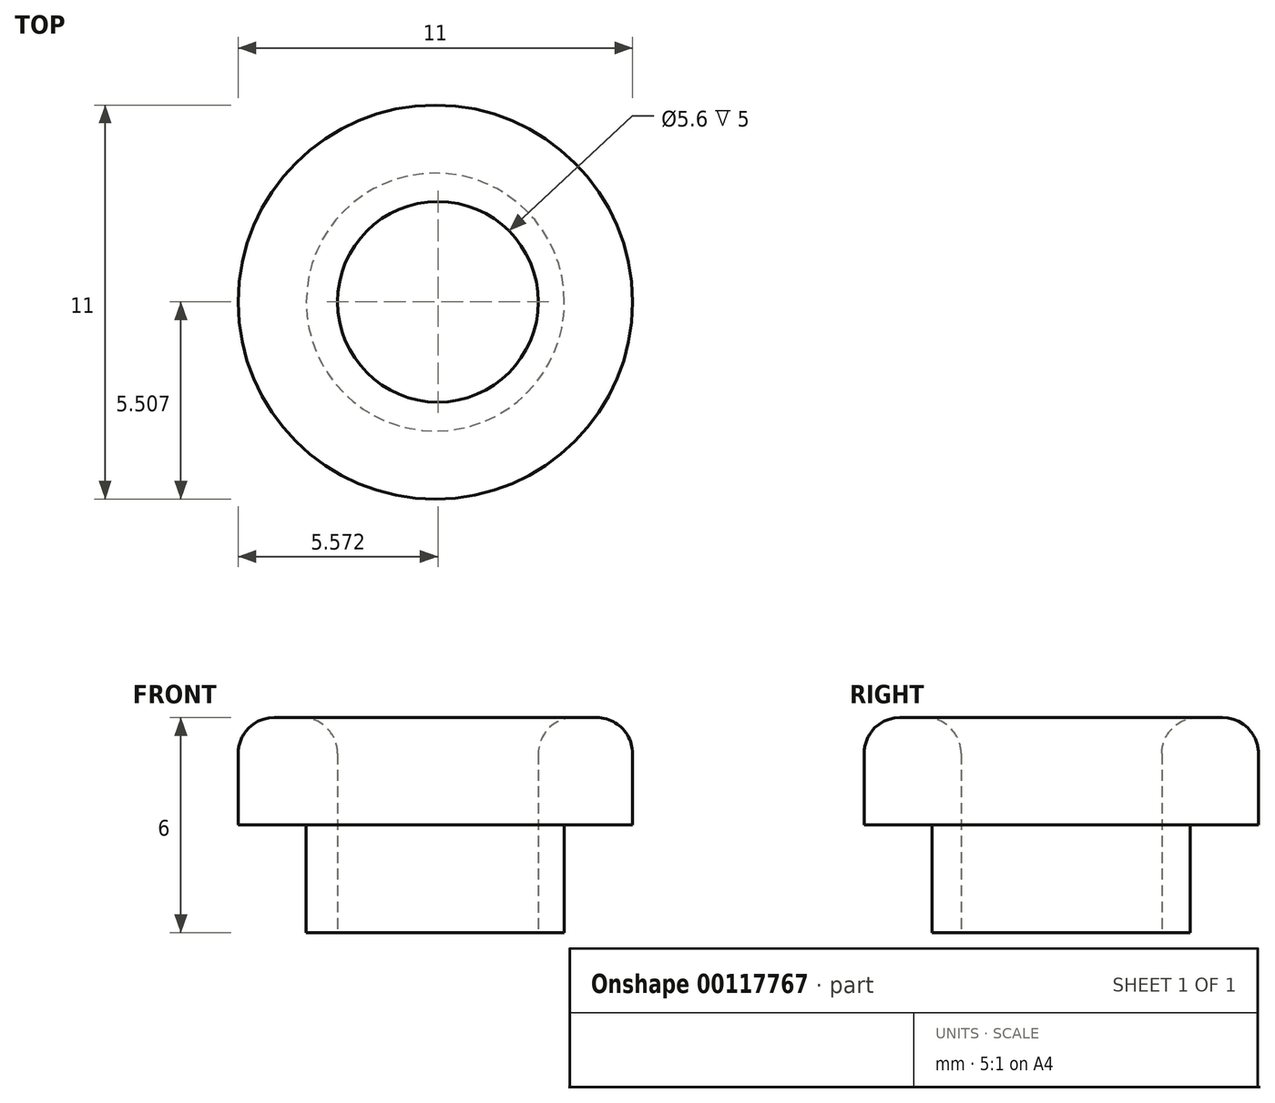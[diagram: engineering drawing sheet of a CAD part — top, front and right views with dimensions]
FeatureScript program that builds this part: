
annotation { "Feature Type Name" : "Feature", "Feature Type Description" : "" }
export const myFeature = defineFeature(function(context is Context, id is Id, definition is map)
    precondition{}
    {
        {
            var Q0;
            Q0=qCreatedBy(makeId("Top.planeOp"),FACE);
            var sketch = newSketch(context, id + "F0", { "sketchPlane" : qUnion([Q0])});
            skCircle(sketch, "E0", {"center": v(0, 0) * mm, "radius": 5.5 * mm});
            skCircle(sketch, "E1", {"center": v(0, 0) * mm, "radius": 3.6 * mm});
            skCircle(sketch, "E2", {"center": v(0.07, 0) * mm, "radius": 2.8 * mm});
            skSolve(sketch);
        }
        {
            var Q0;
            Q0=makeQuery(id+"F0.imprint","IMPRINT",FACE,{"disambiguationData":[TD([[makeQuery(id+"F0.imprint","IMPRINT",EDGE,{"derivedFrom":sQuery(id+"F0.wireOp",EDGE,"E0")}),1.0]])]});
            var Q1;
            Q1=makeQuery(id+"F0.imprint","IMPRINT",FACE,{"disambiguationData":[TD([[makeQuery(id+"F0.imprint","IMPRINT",EDGE,{"derivedFrom":sQuery(id+"F0.wireOp",EDGE,"E1")}),1.0]])]});
            extrude(context, id + "F1", {"entities" : qUnion([Q0, Q1]), "depth" : 3 * mm});
        }
        {
            var Q0;
            Q0=makeQuery(id+"F0.imprint","IMPRINT",FACE,{"disambiguationData":[TD([[makeQuery(id+"F0.imprint","IMPRINT",EDGE,{"derivedFrom":sQuery(id+"F0.wireOp",EDGE,"E1")}),1.0]])]});
            extrude(context, id + "F2", {"entities" : qUnion([Q0]), "operationType" : NewBodyOperationType.ADD, "oppositeDirection" : true, "depth" : 3 * mm});
        }
        {
            var Q0;
            Q0=makeQuery(id+"F1.opExtrude","CAP_EDGE",EDGE,{"disambiguationData":[OSD([sQuery(id+"F0.wireOp",EDGE,"E2")])],"isStart":false});
            var Q1;
            Q1=makeQuery(id+"F1.opExtrude","CAP_EDGE",EDGE,{"disambiguationData":[OSD([sQuery(id+"F0.wireOp",EDGE,"E0")])],"isStart":false});
            fillet(context, id + "F3", {"entities" : qUnion([Q0, Q1]), "radius" : 1 * mm, "tangentPropagation" : true, "allowEdgeOverflow" : false});
        }
    });
